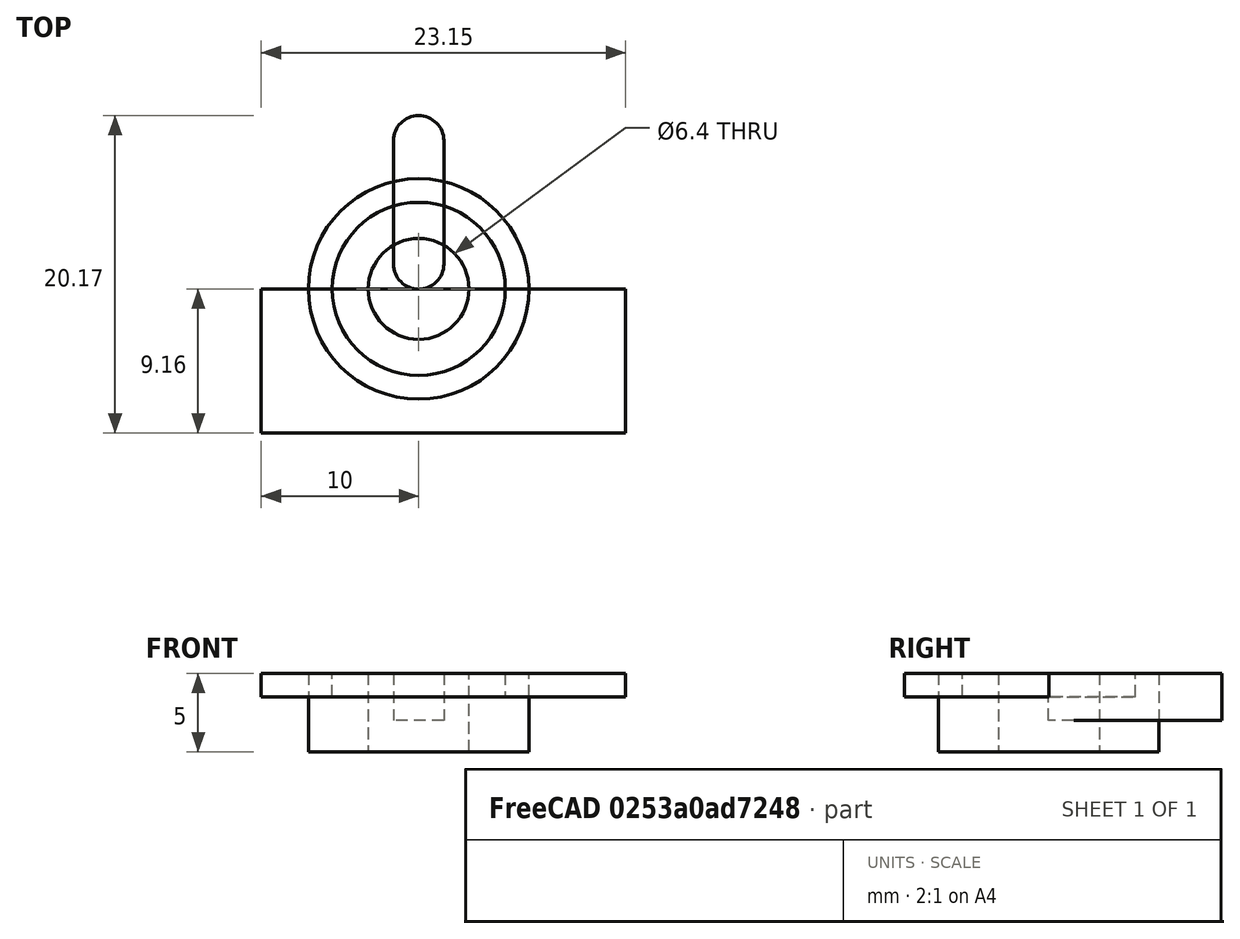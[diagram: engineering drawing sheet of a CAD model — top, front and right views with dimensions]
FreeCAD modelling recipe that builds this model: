
FCSTD DOCUMENT  (FreeCAD 0.16R)
Label: TinyHanger
License: All rights reserved
LicenseURL: http://en.wikipedia.org/wiki/All_rights_reserved
objects: Sketcher::SketchObject×4, PartDesign::Pocket×3, PartDesign::Pad×1, Mesh::Feature×1
note: 12 computed .brp shape members not serialized (recipe doc carries the construction recipe); baked Part::Feature solids carry a one-line shape summary decoded from their .brp

FEATURE [Sketcher::SketchObject] Sketch
  sketch-geometry (2):
    g0: Circle CenterX=0 CenterY=0 CenterZ=0 NormalX=0 NormalY=0 NormalZ=1 Radius=3.2
    g1: Circle CenterX=0 CenterY=0 CenterZ=0 NormalX=0 NormalY=0 NormalZ=1 Radius=7
  constraints (4):
    c: Radius(g0) = 3.2
    c: Coincident(g0,g-1)
    c: Coincident(g1,g-1)
    c: Radius(g1) = 7
FEATURE [PartDesign::Pad] Pad
  Length = 5
  Length2 = 100
  Sketch = -> Sketch
  Type = 0
FEATURE [Sketcher::SketchObject] Sketch001
  Placement = pos=(0,0,5) rot=(0,0,1;0rad)
  Support = -> Pad [Face4]
  sketch-geometry (4):
    g0: ArcOfCircle CenterX=0 CenterY=9.40914 CenterZ=0 NormalX=0 NormalY=0 NormalZ=1 Radius=1.6 StartAngle=0 EndAngle=3.14159
    g1: ArcOfCircle CenterX=0 CenterY=1.58479 CenterZ=0 NormalX=0 NormalY=0 NormalZ=1 Radius=1.6 StartAngle=3.14159 EndAngle=6.28319
    g2: LineSegment StartX=-1.6 StartY=9.40914 StartZ=0 EndX=-1.6 EndY=1.58479 EndZ=0
    g3: LineSegment StartX=1.6 StartY=9.40914 StartZ=0 EndX=1.6 EndY=1.58479 EndZ=0
  constraints (8):
    c: Tangent(g0,g3) = 1.5708
    c: Tangent(g0,g2) = -1.5708
    c: Tangent(g2,g1) = -1.5708
    c: Tangent(g3,g1) = 1.5708
    c: Vertical(g2)
    c: Equal(g0,g1)
    c: Distance(g1,g1) = 3.2
    c: PointOnObject(g1,g-2)
FEATURE [PartDesign::Pocket] Pocket
  Length = 3
  Sketch = -> Sketch001
  Type = 0
FEATURE [Sketcher::SketchObject] Sketch002
  Placement = pos=(0,0,5) rot=(0,0,1;0rad)
  Support = -> Pocket [Face3]
  sketch-geometry (1):
    g0: Circle CenterX=0 CenterY=0 CenterZ=0 NormalX=0 NormalY=0 NormalZ=1 Radius=5.5
  constraints (2):
    c: Coincident(g0,g-1)
    c: Radius(g0) = 5.5
FEATURE [PartDesign::Pocket] Pocket001
  Length = 1.5
  Sketch = -> Sketch002
  Type = 0
FEATURE [Sketcher::SketchObject] Sketch003
  Placement = pos=(0,0,5) rot=(0,0,1;0rad)
  Support = -> Pocket001 [Face3]
  sketch-geometry (4):
    g0: LineSegment StartX=-9.99997 StartY=0 StartZ=0 EndX=13.1495 EndY=0 EndZ=0
    g1: LineSegment StartX=13.1495 StartY=0 StartZ=0 EndX=13.1495 EndY=-9.16319 EndZ=0
    g2: LineSegment StartX=13.1495 StartY=-9.16319 StartZ=0 EndX=-9.99997 EndY=-9.16319 EndZ=0
    g3: LineSegment StartX=-9.99997 StartY=-9.16319 StartZ=0 EndX=-9.99997 EndY=0 EndZ=0
  constraints (9):
    c: Coincident(g0,g1)
    c: Coincident(g1,g2)
    c: Coincident(g2,g3)
    c: Coincident(g3,g0)
    c: Horizontal(g0)
    c: Horizontal(g2)
    c: Vertical(g1)
    c: Vertical(g3)
    c: PointOnObject(g0,g-1)
FEATURE [PartDesign::Pocket] Pocket002
  Length = 1.5
  Sketch = -> Sketch003
  Type = 0
FEATURE [Mesh::Feature] Mesh  label="Pocket002 (Meshed)"
